# Revit family: Table-Teknion-CFTHBH_Figure_Table_Rectangular_Hexa_Panel_Base_Half_Bullnose_Edge-R2023
name_source: partatom
category: Furniture
units: mm (PartAtom-declared; Revit-internal decimal feet)

## family parameters
Always vertical = Yes
Cut with Voids When Loaded = No
Enable Cutting in Views = No
OmniClass Number = 23.40.20.00
OmniClass Title = General Furniture and Specialties
Render Appearance Source = Family Geometry
Room Calculation Point = No
Shared = Yes
Work Plane-Based = No

## types (6) — shared parameters
Assembly Code = E2020200
Manufacturer = Teknion
Manufacturer Fax = 416.661.4586
Part Number = CFTHBH
Product Line = Figure Table
Product Page URL = https://www.teknion.com
Series = Custom Wood Boardroom & Reception Tables
Sustainability Data = https://www.teknion.com
URL = www.teknion.com
Unit Weight URL = http://www.teknion.com
Warranty = http://www.teknion.com
zero-valued in all types: Default Elevation

## per-type parameters (varying)
| type | Depth | Description | Model | Radius Corner | Square Corner |
| 48" Depth, Square Corner Detail | 48 " | Figure Table Rectangular, Hexa Panel Base, Half Bullnose Edge 48D, Square Corner Detail | CFTHBH48__S_ | No | Yes |
| 48" Depth, Radius Corner Detail | 48 " | Figure Table Rectangular, Hexa Panel Base, Half Bullnose Edge 48D, Radius Corner Detail | CFTHBH48__R_ | Yes | No |
| 54" Depth, Square Corner Detail | 54 " | Figure Table Rectangular, Hexa Panel Base, Half Bullnose Edge 54D, Square Corner Detail | CFTHBH54__S_ | No | Yes |
| 54" Depth, Radius Corner Detail | 54 " | Figure Table Rectangular, Hexa Panel Base, Half Bullnose Edge 54D, Radius Corner Detail | CFTHBH54__R_ | Yes | No |
| 60" Depth, Radius Corner Detail | 60 " | Figure Table Rectangular, Hexa Panel Base, Half Bullnose Edge 60D, Radius Corner Detail | CFTHBH60__R_ | Yes | No |
| 60" Depth, Square Corner Detail | 60 " | Figure Table Rectangular, Hexa Panel Base, Half Bullnose Edge 60D, Square Corner Detail | CFTHBH60__S_ | No | Yes |

## geometry (parser evidence)
native form markers: Sweep x3
no freeform markers — native parametric forms only
